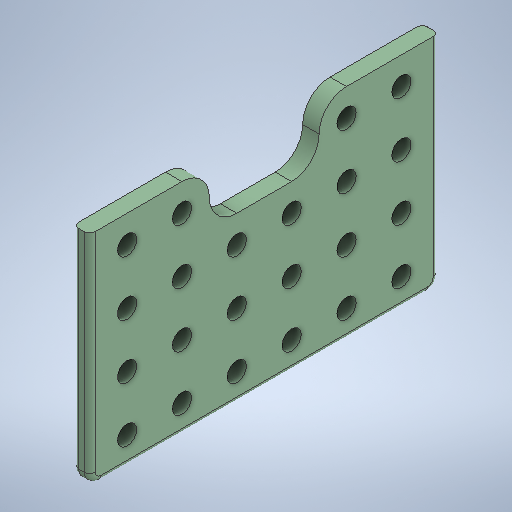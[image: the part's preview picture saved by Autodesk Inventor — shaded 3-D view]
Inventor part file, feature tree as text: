
AUTODESK INVENTOR PART (.ipt)
format: ipt  version: 2025 (Build 290162000, 162)  size: 729,088 bytes
history: native  units: mm
features: fillet x3, extrude x2, sketch x2
ambient origin geometry x8: Origin, YZ Plane, XZ Plane, XY Plane, X Axis, Y Axis, Z Axis, Center Point
bodies: Solide1 (feature_tree)
feature tree (7):
  extrude  "Extrusion1"  Depth=3.0mm
  fillet  "Congé1"  Radius=63.6mm
  fillet  "Congé2"  Radius=40.0mm
  extrude  "Extrusion2"  Depth=2.0mm
  fillet  "Congé3"  Radius=1.0mm
  sketch  "Esquisse1"
  sketch  "Esquisse2"
